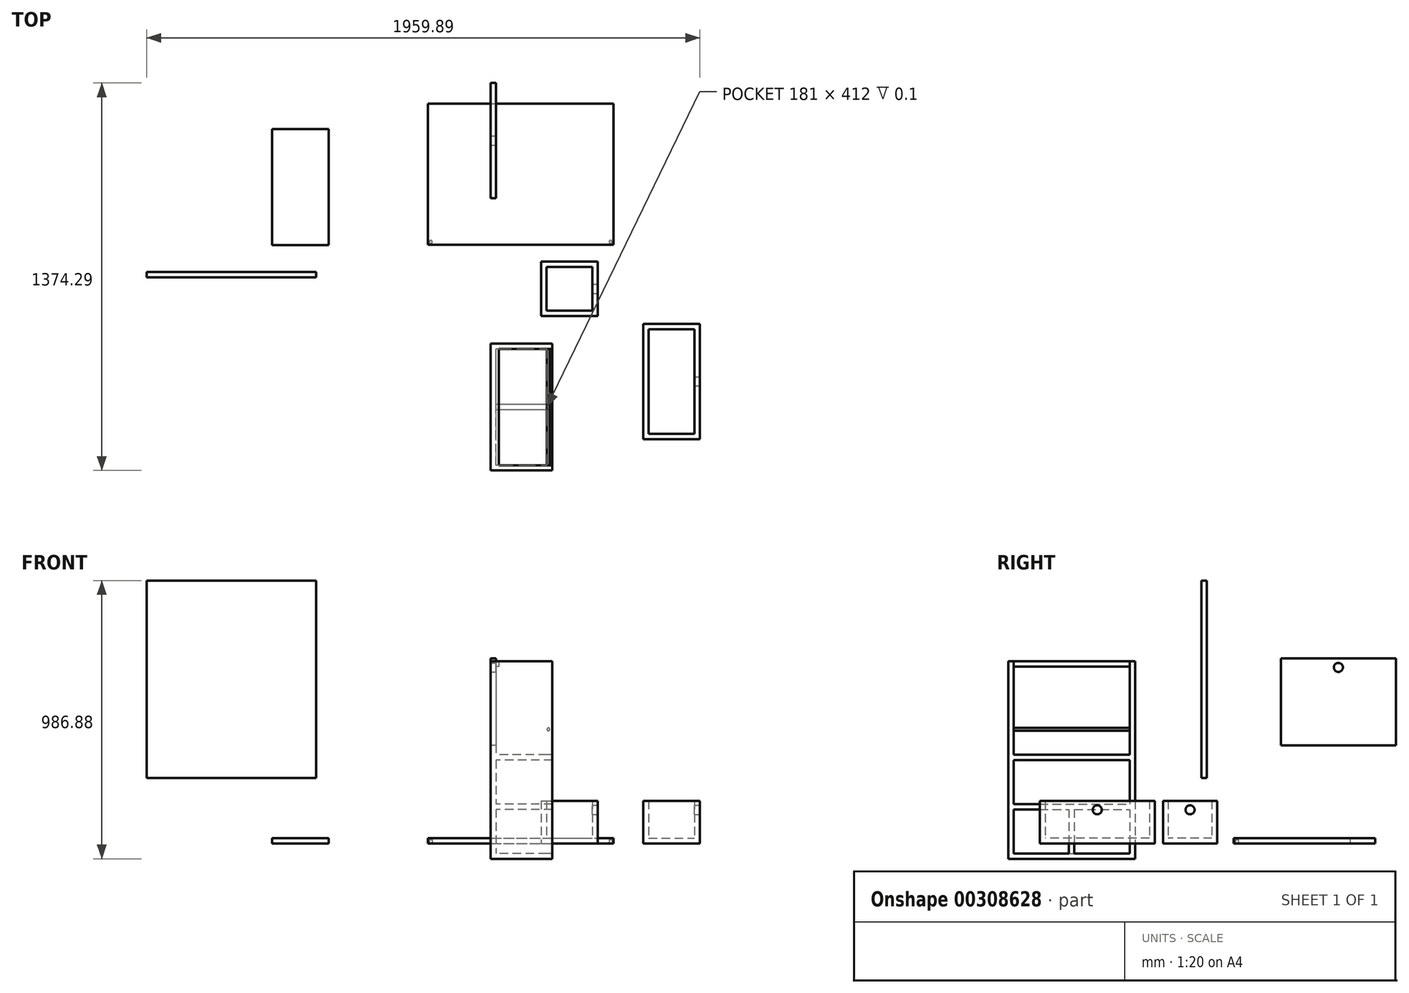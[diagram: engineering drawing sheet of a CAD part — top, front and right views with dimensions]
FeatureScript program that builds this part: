
annotation { "Feature Type Name" : "Feature", "Feature Type Description" : "" }
export const myFeature = defineFeature(function(context is Context, id is Id, definition is map)
    precondition{}
    {
        {
            var Q0;
            Q0=qCreatedBy(makeId("Right.planeOp"),FACE);
            var sketch = newSketch(context, id + "F0", { "sketchPlane" : qUnion([Q0])});
            skLineSegment(sketch, "E0.bottom", {"start": v(-703.87, 646.4) * mm, "end": v(-253.87, 646.4) * mm});
            skLineSegment(sketch, "E0.top", {"start": v(-703.87, -53.6) * mm, "end": v(-253.87, -53.6) * mm});
            skLineSegment(sketch, "E0.left", {"start": v(-703.87, 646.4) * mm, "end": v(-703.87, -53.6) * mm});
            skLineSegment(sketch, "E0.right", {"start": v(-253.87, 646.4) * mm, "end": v(-253.87, -53.6) * mm});
            skSolve(sketch);
        }
        {
            var Q0;
            Q0=qSketchRegion(id+"F0",true);
            extrude(context, id + "F1", {"entities" : qUnion([Q0]), "depth" : 19 * mm});
        }
        {
            var Q0;
            Q0=makeQuery(id+"F1.opExtrude","CAP_FACE",FACE,{"disambiguationData":[OSD([sQuery(id+"F0.wireOp",EDGE,"E0.bottom"),sQuery(id+"F0.wireOp",EDGE,"E0.top"),sQuery(id+"F0.wireOp",EDGE,"E0.left"),sQuery(id+"F0.wireOp",EDGE,"E0.right")])],"isStart":false});
            var sketch = newSketch(context, id + "F2", { "sketchPlane" : qUnion([Q0])});
            skLineSegment(sketch, "E1.bottom", {"start": v(-703.87, 646.4) * mm, "end": v(-684.87, 646.4) * mm});
            skLineSegment(sketch, "E1.top", {"start": v(-703.87, -53.6) * mm, "end": v(-684.87, -53.6) * mm});
            skLineSegment(sketch, "E1.left", {"start": v(-703.87, 646.4) * mm, "end": v(-703.87, -53.6) * mm});
            skLineSegment(sketch, "E1.right", {"start": v(-684.87, 646.4) * mm, "end": v(-684.87, -53.6) * mm});
            skSolve(sketch);
        }
        {
            var Q0;
            Q0=qSketchRegion(id+"F2",true);
            extrude(context, id + "F3", {"entities" : qUnion([Q0]), "operationType" : NewBodyOperationType.ADD, "depth" : 200 * mm});
        }
        {
            var Q0;
            Q0=makeQuery(id+"F1.opExtrude","CAP_FACE",FACE,{"disambiguationData":[OSD([sQuery(id+"F0.wireOp",EDGE,"E0.bottom"),sQuery(id+"F0.wireOp",EDGE,"E0.top"),sQuery(id+"F0.wireOp",EDGE,"E0.left"),sQuery(id+"F0.wireOp",EDGE,"E0.right")])],"isStart":false});
            var sketch = newSketch(context, id + "F4", { "sketchPlane" : qUnion([Q0])});
            skLineSegment(sketch, "E2.bottom", {"start": v(-253.87, 646.4) * mm, "end": v(-272.87, 646.4) * mm});
            skLineSegment(sketch, "E2.top", {"start": v(-253.87, -53.6) * mm, "end": v(-272.87, -53.6) * mm});
            skLineSegment(sketch, "E2.left", {"start": v(-253.87, 646.4) * mm, "end": v(-253.87, -53.6) * mm});
            skLineSegment(sketch, "E2.right", {"start": v(-272.87, 646.4) * mm, "end": v(-272.87, -53.6) * mm});
            skSolve(sketch);
        }
        {
            var Q0;
            Q0=makeQuery(id+"F4.imprint","IMPRINT",FACE,{"disambiguationData":[TD([[makeQuery(id+"F4.imprint","IMPRINT",EDGE,{"derivedFrom":sQuery(id+"F4.wireOp",EDGE,"E2.bottom")}),-1.0]])]});
            extrude(context, id + "F5", {"entities" : qUnion([Q0]), "operationType" : NewBodyOperationType.ADD, "depth" : 200 * mm});
        }
        {
            var Q0;
            Q0=makeQuery(id+"F1.opExtrude","CAP_FACE",FACE,{"disambiguationData":[OSD([sQuery(id+"F0.wireOp",EDGE,"E0.bottom"),sQuery(id+"F0.wireOp",EDGE,"E0.top"),sQuery(id+"F0.wireOp",EDGE,"E0.left"),sQuery(id+"F0.wireOp",EDGE,"E0.right")])],"isStart":false});
            var sketch = newSketch(context, id + "F6", { "sketchPlane" : qUnion([Q0])});
            skLineSegment(sketch, "E3.bottom", {"start": v(-684.87, 646.4) * mm, "end": v(-272.87, 646.4) * mm});
            skLineSegment(sketch, "E3.top", {"start": v(-684.87, 627.4) * mm, "end": v(-272.87, 627.4) * mm});
            skLineSegment(sketch, "E3.left", {"start": v(-684.87, 646.4) * mm, "end": v(-684.87, 627.4) * mm});
            skLineSegment(sketch, "E3.right", {"start": v(-272.87, 646.4) * mm, "end": v(-272.87, 627.4) * mm});
            skSolve(sketch);
        }
        {
            var Q0;
            Q0=makeQuery(id+"F6.imprint","IMPRINT",FACE,{"disambiguationData":[TD([[makeQuery(id+"F6.imprint","IMPRINT",EDGE,{"derivedFrom":sQuery(id+"F6.wireOp",EDGE,"E3.bottom")}),-1.0]])]});
            extrude(context, id + "F7", {"entities" : qUnion([Q0]), "operationType" : NewBodyOperationType.ADD, "depth" : 10 * mm});
        }
        {
            var Q0;
            Q0=makeQuery(id+"F1.opExtrude","CAP_FACE",FACE,{"disambiguationData":[OSD([sQuery(id+"F0.wireOp",EDGE,"E0.bottom"),sQuery(id+"F0.wireOp",EDGE,"E0.top"),sQuery(id+"F0.wireOp",EDGE,"E0.left"),sQuery(id+"F0.wireOp",EDGE,"E0.right")])],"isStart":false});
            var sketch = newSketch(context, id + "F8", { "sketchPlane" : qUnion([Q0])});
            skLineSegment(sketch, "E4.bottom", {"start": v(-684.87, -53.6) * mm, "end": v(-272.87, -53.6) * mm});
            skLineSegment(sketch, "E4.top", {"start": v(-684.87, -34.6) * mm, "end": v(-272.87, -34.6) * mm});
            skLineSegment(sketch, "E4.left", {"start": v(-684.87, -53.6) * mm, "end": v(-684.87, -34.6) * mm});
            skLineSegment(sketch, "E4.right", {"start": v(-272.87, -53.6) * mm, "end": v(-272.87, -34.6) * mm});
            skSolve(sketch);
        }
        {
            var Q0;
            Q0=qSketchRegion(id+"F8",true);
            extrude(context, id + "F9", {"entities" : qUnion([Q0]), "operationType" : NewBodyOperationType.ADD, "depth" : 200 * mm});
        }
        {
            var Q0;
            Q0=makeQuery(id+"F9.opExtrude","SWEPT_FACE",FACE,{"disambiguationData":[OSD([sQuery(id+"F8.wireOp",EDGE,"E4.top")])]});
            var sketch = newSketch(context, id + "F10", { "sketchPlane" : qUnion([Q0])});
            skLineSegment(sketch, "E5.bottom", {"start": v(219, -684.87) * mm, "end": v(200, -684.87) * mm});
            skLineSegment(sketch, "E5.top", {"start": v(219, -272.87) * mm, "end": v(200, -272.87) * mm});
            skLineSegment(sketch, "E5.left", {"start": v(219, -684.87) * mm, "end": v(219, -272.87) * mm});
            skLineSegment(sketch, "E5.right", {"start": v(200, -684.87) * mm, "end": v(200, -272.87) * mm});
            skSolve(sketch);
        }
        {
            var Q0;
            Q0=qSketchRegion(id+"F10",true);
            extrude(context, id + "F11", {"entities" : qUnion([Q0]), "operationType" : NewBodyOperationType.ADD, "depth" : 0.1 * mm});
        }
        {
            var Q0;
            Q0=makeQuery(id+"F1.opExtrude","CAP_FACE",FACE,{"disambiguationData":[OSD([sQuery(id+"F0.wireOp",EDGE,"E0.bottom"),sQuery(id+"F0.wireOp",EDGE,"E0.top"),sQuery(id+"F0.wireOp",EDGE,"E0.left"),sQuery(id+"F0.wireOp",EDGE,"E0.right")])],"isStart":false});
            var sketch = newSketch(context, id + "F12", { "sketchPlane" : qUnion([Q0])});
            skLineSegment(sketch, "E6.bottom", {"start": v(-684.87, 296.4) * mm, "end": v(-272.87, 296.4) * mm});
            skLineSegment(sketch, "E6.top", {"start": v(-684.87, 315.4) * mm, "end": v(-272.87, 315.4) * mm});
            skLineSegment(sketch, "E6.left", {"start": v(-684.87, 296.4) * mm, "end": v(-684.87, 315.4) * mm});
            skLineSegment(sketch, "E6.right", {"start": v(-272.87, 296.4) * mm, "end": v(-272.87, 315.4) * mm});
            skSolve(sketch);
        }
        {
            var Q0;
            Q0=qSketchRegion(id+"F12",true);
            extrude(context, id + "F13", {"entities" : qUnion([Q0]), "operationType" : NewBodyOperationType.ADD, "depth" : 200 * mm});
        }
        {
            var Q0;
            Q0=makeQuery(id+"F13.opExtrude","SWEPT_FACE",FACE,{"disambiguationData":[OSD([sQuery(id+"F12.wireOp",EDGE,"E6.top")])]});
            var sketch = newSketch(context, id + "F14", { "sketchPlane" : qUnion([Q0])});
            skLineSegment(sketch, "E7.bottom", {"start": v(219, -272.87) * mm, "end": v(200, -272.87) * mm});
            skLineSegment(sketch, "E7.top", {"start": v(219, -684.87) * mm, "end": v(200, -684.87) * mm});
            skLineSegment(sketch, "E7.left", {"start": v(219, -272.87) * mm, "end": v(219, -684.87) * mm});
            skLineSegment(sketch, "E7.right", {"start": v(200, -272.87) * mm, "end": v(200, -684.87) * mm});
            skSolve(sketch);
        }
        {
            var Q0;
            Q0=qSketchRegion(id+"F14",true);
            extrude(context, id + "F15", {"entities" : qUnion([Q0]), "operationType" : NewBodyOperationType.ADD, "depth" : 0.1 * mm});
        }
        {
            var Q0;
            Q0=qCreatedBy(makeId("Top.planeOp"),FACE);
            var sketch = newSketch(context, id + "F16", { "sketchPlane" : qUnion([Q0])});
            skLineSegment(sketch, "E8.bottom", {"start": v(-221.88, 597.16) * mm, "end": v(435.12, 597.16) * mm});
            skLineSegment(sketch, "E8.top", {"start": v(-221.88, 97.16) * mm, "end": v(435.12, 97.16) * mm});
            skLineSegment(sketch, "E8.left", {"start": v(-221.88, 597.16) * mm, "end": v(-221.88, 97.16) * mm});
            skLineSegment(sketch, "E8.right", {"start": v(435.12, 597.16) * mm, "end": v(435.12, 97.16) * mm});
            skSolve(sketch);
        }
        {
            var Q0;
            Q0=makeQuery(id+"F16.imprint","IMPRINT",FACE,{"disambiguationData":[TD([[makeQuery(id+"F16.imprint","IMPRINT",EDGE,{"derivedFrom":sQuery(id+"F16.wireOp",EDGE,"E8.bottom")}),-1.0]])]});
            extrude(context, id + "F17", {"entities" : qUnion([Q0]), "depth" : 19 * mm});
        }
        {
            var Q0;
            Q0=qCreatedBy(makeId("Front.planeOp"),FACE);
            var sketch = newSketch(context, id + "F18", { "sketchPlane" : qUnion([Q0])});
            skLineSegment(sketch, "E9.bottom", {"start": v(-1218.5, 933.28) * mm, "end": v(-618.5, 933.28) * mm});
            skLineSegment(sketch, "E9.top", {"start": v(-1218.5, 233.28) * mm, "end": v(-618.5, 233.28) * mm});
            skLineSegment(sketch, "E9.left", {"start": v(-1218.5, 933.28) * mm, "end": v(-1218.5, 233.28) * mm});
            skLineSegment(sketch, "E9.right", {"start": v(-618.5, 933.28) * mm, "end": v(-618.5, 233.28) * mm});
            skSolve(sketch);
        }
        {
            var Q0;
            Q0=qSketchRegion(id+"F18",true);
            extrude(context, id + "F19", {"entities" : qUnion([Q0]), "depth" : 19 * mm});
        }
        {
            var Q0;
            Q0=makeQuery(id+"F7.boolean.opBoolean","MERGE",FACE,{"derivedFrom":[makeQuery(id+"F5.boolean.opBoolean","MERGE",FACE,{"derivedFrom":[makeQuery(id+"F3.boolean.opBoolean","MERGE",FACE,{"derivedFrom":[makeQuery(id+"F1.opExtrude","SWEPT_FACE",FACE,{"disambiguationData":[OSD([sQuery(id+"F0.wireOp",EDGE,"E0.bottom")])]}),makeQuery(id+"F3.opExtrude","SWEPT_FACE",FACE,{"disambiguationData":[OSD([sQuery(id+"F2.wireOp",EDGE,"E1.bottom")])]})]}),makeQuery(id+"F5.opExtrude","SWEPT_FACE",FACE,{"disambiguationData":[OSD([sQuery(id+"F4.wireOp",EDGE,"E2.bottom")])]})]}),makeQuery(id+"F7.opExtrude","SWEPT_FACE",FACE,{"disambiguationData":[OSD([sQuery(id+"F6.wireOp",EDGE,"E3.bottom")])]})]});
            var sketch = newSketch(context, id + "F20", { "sketchPlane" : qUnion([Q0])});
            skCircle(sketch, "E10", {"center": v(169, -303.87) * mm, "radius": 5 * mm});
            skSolve(sketch);
        }
        {
            var Q0;
            Q0=makeQuery(id+"F20.imprint","IMPRINT",FACE,{"disambiguationData":[TD([[makeQuery(id+"F20.imprint","IMPRINT",EDGE,{"derivedFrom":sQuery(id+"F20.wireOp",EDGE,"E10")}),1.0]])]});
            extrude(context, id + "F21", {"entities" : qUnion([Q0]), "operationType" : NewBodyOperationType.REMOVE, "oppositeDirection" : true, "depth" : 15 * mm});
        }
        {
            var Q0;
            Q0=makeQuery(id+"F17.opExtrude","CAP_FACE",FACE,{"disambiguationData":[OSD([sQuery(id+"F16.wireOp",EDGE,"E8.bottom"),sQuery(id+"F16.wireOp",EDGE,"E8.top"),sQuery(id+"F16.wireOp",EDGE,"E8.left"),sQuery(id+"F16.wireOp",EDGE,"E8.right")])],"isStart":true});
            var sketch = newSketch(context, id + "F22", { "sketchPlane" : qUnion([Q0])});
            skCircle(sketch, "E11", {"center": v(425.12, -107.16) * mm, "radius": 5 * mm});
            skSolve(sketch);
        }
        {
            var Q0;
            Q0=qSketchRegion(id+"F22",true);
            extrude(context, id + "F23", {"entities" : qUnion([Q0]), "operationType" : NewBodyOperationType.REMOVE, "oppositeDirection" : true, "depth" : 15 * mm});
        }
        {
            var Q0;
            Q0=makeQuery(id+"F7.boolean.opBoolean","MERGE",FACE,{"derivedFrom":[makeQuery(id+"F5.boolean.opBoolean","MERGE",FACE,{"derivedFrom":[makeQuery(id+"F3.boolean.opBoolean","MERGE",FACE,{"derivedFrom":[makeQuery(id+"F1.opExtrude","SWEPT_FACE",FACE,{"disambiguationData":[OSD([sQuery(id+"F0.wireOp",EDGE,"E0.bottom")])]}),makeQuery(id+"F3.opExtrude","SWEPT_FACE",FACE,{"disambiguationData":[OSD([sQuery(id+"F2.wireOp",EDGE,"E1.bottom")])]})]}),makeQuery(id+"F5.opExtrude","SWEPT_FACE",FACE,{"disambiguationData":[OSD([sQuery(id+"F4.wireOp",EDGE,"E2.bottom")])]})]}),makeQuery(id+"F7.opExtrude","SWEPT_FACE",FACE,{"disambiguationData":[OSD([sQuery(id+"F6.wireOp",EDGE,"E3.bottom")])]})]});
            var sketch = newSketch(context, id + "F24", { "sketchPlane" : qUnion([Q0])});
            skCircle(sketch, "E12", {"center": v(169, -653.87) * mm, "radius": 5 * mm});
            skSolve(sketch);
        }
        {
            var Q0;
            Q0=makeQuery(id+"F24.imprint","IMPRINT",FACE,{"disambiguationData":[TD([[makeQuery(id+"F24.imprint","IMPRINT",EDGE,{"derivedFrom":sQuery(id+"F24.wireOp",EDGE,"E12")}),1.0]])]});
            extrude(context, id + "F25", {"entities" : qUnion([Q0]), "operationType" : NewBodyOperationType.REMOVE, "oppositeDirection" : true, "depth" : 15 * mm});
        }
        {
            var Q0;
            Q0=makeQuery(id+"F17.opExtrude","CAP_FACE",FACE,{"disambiguationData":[OSD([sQuery(id+"F16.wireOp",EDGE,"E8.bottom"),sQuery(id+"F16.wireOp",EDGE,"E8.top"),sQuery(id+"F16.wireOp",EDGE,"E8.left"),sQuery(id+"F16.wireOp",EDGE,"E8.right")])],"isStart":true});
            var sketch = newSketch(context, id + "F26", { "sketchPlane" : qUnion([Q0])});
            skCircle(sketch, "E13", {"center": v(-211.88, -107.16) * mm, "radius": 5 * mm});
            skSolve(sketch);
        }
        {
            var Q0;
            Q0=makeQuery(id+"F26.imprint","IMPRINT",FACE,{"disambiguationData":[TD([[makeQuery(id+"F26.imprint","IMPRINT",EDGE,{"derivedFrom":sQuery(id+"F26.wireOp",EDGE,"E13")}),1.0]])]});
            extrude(context, id + "F27", {"entities" : qUnion([Q0]), "operationType" : NewBodyOperationType.REMOVE, "oppositeDirection" : true, "depth" : 15 * mm});
        }
        {
            var Q0;
            {var subQ0=sQuery(id+"F4.wireOp",EDGE,"E2.right");var subQ3=sQuery(id+"F0.wireOp",EDGE,"E0.bottom");Q0=makeQuery(id+"F13.boolean.opBoolean","SPLIT",FACE,{"disambiguationData":[TD([makeQuery(id+"F1.opExtrude","SWEPT_FACE",FACE,{"disambiguationData":[OSD([subQ3])]})])],"derivedFrom":makeQuery(id+"F5.opExtrude","SWEPT_FACE",FACE,{"disambiguationData":[OSD([subQ0])]})});}
            var sketch = newSketch(context, id + "F28", { "sketchPlane" : qUnion([Q0])});
            skCircle(sketch, "E14", {"center": v(205, 405.5) * mm, "radius": 5 * mm});
            skSolve(sketch);
        }
        {
            var Q0;
            Q0=makeQuery(id+"F28.imprint","IMPRINT",FACE,{"disambiguationData":[TD([[makeQuery(id+"F28.imprint","IMPRINT",EDGE,{"derivedFrom":sQuery(id+"F28.wireOp",EDGE,"E14")}),1.0]])]});
            extrude(context, id + "F29", {"entities" : qUnion([Q0]), "operationType" : NewBodyOperationType.ADD, "depth" : 430 * mm});
        }
        {
            var Q0;
            Q0=makeQuery(id+"F13.boolean.opBoolean","SPLIT",FACE,{"disambiguationData":[TD([makeQuery(id+"F9.opExtrude","SWEPT_FACE",FACE,{"disambiguationData":[OSD([sQuery(id+"F8.wireOp",EDGE,"E4.top")])]})])],"derivedFrom":makeQuery(id+"F1.opExtrude","CAP_FACE",FACE,{"disambiguationData":[OSD([sQuery(id+"F0.wireOp",EDGE,"E0.bottom"),sQuery(id+"F0.wireOp",EDGE,"E0.top"),sQuery(id+"F0.wireOp",EDGE,"E0.left"),sQuery(id+"F0.wireOp",EDGE,"E0.right")])],"isStart":false})});
            var sketch = newSketch(context, id + "F30", { "sketchPlane" : qUnion([Q0])});
            skLineSegment(sketch, "E15.bottom", {"start": v(-684.87, 121.45) * mm, "end": v(-272.87, 121.45) * mm});
            skLineSegment(sketch, "E15.top", {"start": v(-684.87, 140.45) * mm, "end": v(-272.87, 140.45) * mm});
            skLineSegment(sketch, "E15.left", {"start": v(-684.87, 121.45) * mm, "end": v(-684.87, 140.45) * mm});
            skLineSegment(sketch, "E15.right", {"start": v(-272.87, 121.45) * mm, "end": v(-272.87, 140.45) * mm});
            skSolve(sketch);
        }
        {
            var Q0;
            Q0=qSketchRegion(id+"F30",true);
            var Q1;
            Q1=makeQuery(id+"F30.imprint","IMPRINT",FACE,{"disambiguationData":[TD([[makeQuery(id+"F30.imprint","IMPRINT",EDGE,{"derivedFrom":sQuery(id+"F30.wireOp",EDGE,"E15.bottom")}),1.0]])]});
            extrude(context, id + "F31", {"entities" : qUnion([Q0, Q1]), "operationType" : NewBodyOperationType.ADD, "depth" : 200 * mm});
        }
        {
            var Q0;
            {var subQ1=makeQuery(id+"F13.opExtrude","SWEPT_FACE",FACE,{"disambiguationData":[OSD([sQuery(id+"F12.wireOp",EDGE,"E6.bottom")])]});Q0=makeQuery(id+"F31.boolean.opBoolean","SPLIT",FACE,{"disambiguationData":[TD([subQ1])],"derivedFrom":makeQuery(id+"F13.boolean.opBoolean","SPLIT",FACE,{"disambiguationData":[TD([makeQuery(id+"F9.opExtrude","SWEPT_FACE",FACE,{"disambiguationData":[OSD([sQuery(id+"F8.wireOp",EDGE,"E4.top")])]})])],"derivedFrom":makeQuery(id+"F1.opExtrude","CAP_FACE",FACE,{"disambiguationData":[OSD([sQuery(id+"F0.wireOp",EDGE,"E0.bottom"),sQuery(id+"F0.wireOp",EDGE,"E0.top"),sQuery(id+"F0.wireOp",EDGE,"E0.left"),sQuery(id+"F0.wireOp",EDGE,"E0.right")])],"isStart":false})})});}
            var sketch = newSketch(context, id + "F32", { "sketchPlane" : qUnion([Q0])});
            skLineSegment(sketch, "E16.bottom", {"start": v(-488.37, 296.4) * mm, "end": v(-469.37, 296.4) * mm});
            skLineSegment(sketch, "E16.top", {"start": v(-488.37, -34.5) * mm, "end": v(-469.37, -34.5) * mm});
            skLineSegment(sketch, "E16.left", {"start": v(-488.37, 296.4) * mm, "end": v(-488.37, -34.5) * mm});
            skLineSegment(sketch, "E16.right", {"start": v(-469.37, 296.4) * mm, "end": v(-469.37, -34.5) * mm});
            skSolve(sketch);
        }
        {
            var Q0;
            {var subQ0=sQuery(id+"F32.wireOp",EDGE,"E16.top");Q0=makeQuery(id+"F32.imprint","IMPRINT",FACE,{"disambiguationData":[TD([[makeQuery(id+"F32.imprint","IMPRINT",EDGE,{"derivedFrom":subQ0}),1.0]])]});}
            extrude(context, id + "F33", {"entities" : qUnion([Q0]), "operationType" : NewBodyOperationType.ADD, "depth" : 200 * mm});
        }
        {
            var Q0;
            Q0=qCreatedBy(makeId("Top.planeOp"),FACE);
            var sketch = newSketch(context, id + "F34", { "sketchPlane" : qUnion([Q0])});
            skLineSegment(sketch, "E17.bottom", {"start": v(179.4, 36.97) * mm, "end": v(379.4, 36.97) * mm});
            skLineSegment(sketch, "E17.top", {"start": v(179.4, -155.53) * mm, "end": v(379.4, -155.53) * mm});
            skLineSegment(sketch, "E17.left", {"start": v(179.4, 36.97) * mm, "end": v(179.4, -155.53) * mm});
            skLineSegment(sketch, "E17.right", {"start": v(379.4, 36.97) * mm, "end": v(379.4, -155.53) * mm});
            skSolve(sketch);
        }
        {
            var Q0;
            Q0=qSketchRegion(id+"F34",true);
            extrude(context, id + "F35", {"entities" : qUnion([Q0]), "depth" : 19 * mm});
        }
        {
            var Q0;
            Q0=makeQuery(id+"F35.opExtrude","CAP_FACE",FACE,{"disambiguationData":[OSD([sQuery(id+"F34.wireOp",EDGE,"E17.bottom"),sQuery(id+"F34.wireOp",EDGE,"E17.top"),sQuery(id+"F34.wireOp",EDGE,"E17.left"),sQuery(id+"F34.wireOp",EDGE,"E17.right")])],"isStart":false});
            var sketch = newSketch(context, id + "F36", { "sketchPlane" : qUnion([Q0])});
            skLineSegment(sketch, "E18.bottom", {"start": v(179.4, 36.97) * mm, "end": v(379.4, 36.97) * mm});
            skLineSegment(sketch, "E18.top", {"start": v(179.4, -155.53) * mm, "end": v(379.4, -155.53) * mm});
            skLineSegment(sketch, "E18.left", {"start": v(179.4, 36.97) * mm, "end": v(179.4, -155.53) * mm});
            skLineSegment(sketch, "E18.right", {"start": v(379.4, 36.97) * mm, "end": v(379.4, -155.53) * mm});
            skLineSegment(sketch, "E19.bottom", {"start": v(198.4, 17.97) * mm, "end": v(360.4, 17.97) * mm});
            skLineSegment(sketch, "E19.top", {"start": v(198.4, -136.53) * mm, "end": v(360.4, -136.53) * mm});
            skLineSegment(sketch, "E19.left", {"start": v(198.4, 17.97) * mm, "end": v(198.4, -136.53) * mm});
            skLineSegment(sketch, "E19.right", {"start": v(360.4, 17.97) * mm, "end": v(360.4, -136.53) * mm});
            skSolve(sketch);
        }
        {
            var Q0;
            Q0=makeQuery(id+"F36.imprint","IMPRINT",FACE,{"disambiguationData":[TD([[makeQuery(id+"F36.imprint","IMPRINT",EDGE,{"derivedFrom":sQuery(id+"F36.wireOp",EDGE,"E18.bottom")}),-1.0]])]});
            extrude(context, id + "F37", {"entities" : qUnion([Q0]), "operationType" : NewBodyOperationType.ADD, "depth" : 132.95 * mm});
        }
        {
            var Q0;
            Q0=makeQuery(id+"F37.boolean.opBoolean","MERGE",FACE,{"derivedFrom":[makeQuery(id+"F35.opExtrude","SWEPT_FACE",FACE,{"disambiguationData":[OSD([sQuery(id+"F34.wireOp",EDGE,"E17.right")])]}),makeQuery(id+"F37.opExtrude","SWEPT_FACE",FACE,{"disambiguationData":[OSD([sQuery(id+"F36.wireOp",EDGE,"E18.right")])]})]});
            var sketch = newSketch(context, id + "F38", { "sketchPlane" : qUnion([Q0])});
            skCircle(sketch, "E20", {"center": v(-59.28, 119.95) * mm, "radius": 16 * mm});
            skPoint(sketch, "E20.centerSnap0", {"position": v(-59.28, 151.95) * mm});
            skSolve(sketch);
        }
        {
            var Q0;
            Q0=makeQuery(id+"F38.imprint","IMPRINT",FACE,{"disambiguationData":[TD([[makeQuery(id+"F38.imprint","IMPRINT",EDGE,{"derivedFrom":sQuery(id+"F38.wireOp",EDGE,"E20")}),1.0]])]});
            extrude(context, id + "F39", {"entities" : qUnion([Q0]), "operationType" : NewBodyOperationType.REMOVE, "oppositeDirection" : true, "depth" : 25 * mm});
        }
        {
            var Q0;
            Q0=qCreatedBy(makeId("Top.planeOp"),FACE);
            var sketch = newSketch(context, id + "F40", { "sketchPlane" : qUnion([Q0])});
            skLineSegment(sketch, "E21.bottom", {"start": v(541.4, -184.16) * mm, "end": v(741.4, -184.16) * mm});
            skLineSegment(sketch, "E21.top", {"start": v(541.4, -592.16) * mm, "end": v(741.4, -592.16) * mm});
            skLineSegment(sketch, "E21.left", {"start": v(541.4, -184.16) * mm, "end": v(541.4, -592.16) * mm});
            skLineSegment(sketch, "E21.right", {"start": v(741.4, -184.16) * mm, "end": v(741.4, -592.16) * mm});
            skSolve(sketch);
        }
        {
            var Q0;
            Q0=makeQuery(id+"F40.imprint","IMPRINT",FACE,{"disambiguationData":[TD([[makeQuery(id+"F40.imprint","IMPRINT",EDGE,{"derivedFrom":sQuery(id+"F40.wireOp",EDGE,"E21.bottom")}),-1.0]])]});
            extrude(context, id + "F41", {"entities" : qUnion([Q0]), "depth" : 19 * mm});
        }
        {
            var Q0;
            Q0=makeQuery(id+"F41.opExtrude","CAP_FACE",FACE,{"disambiguationData":[OSD([sQuery(id+"F40.wireOp",EDGE,"E21.bottom"),sQuery(id+"F40.wireOp",EDGE,"E21.top"),sQuery(id+"F40.wireOp",EDGE,"E21.left"),sQuery(id+"F40.wireOp",EDGE,"E21.right")])],"isStart":false});
            var sketch = newSketch(context, id + "F42", { "sketchPlane" : qUnion([Q0])});
            skLineSegment(sketch, "E22.bottom", {"start": v(541.4, -184.16) * mm, "end": v(741.4, -184.16) * mm});
            skLineSegment(sketch, "E22.top", {"start": v(541.4, -592.16) * mm, "end": v(741.4, -592.16) * mm});
            skLineSegment(sketch, "E22.left", {"start": v(541.4, -184.16) * mm, "end": v(541.4, -592.16) * mm});
            skLineSegment(sketch, "E22.right", {"start": v(741.4, -184.16) * mm, "end": v(741.4, -592.16) * mm});
            skLineSegment(sketch, "E23.bottom", {"start": v(560.4, -203.16) * mm, "end": v(722.4, -203.16) * mm});
            skLineSegment(sketch, "E23.top", {"start": v(560.4, -573.16) * mm, "end": v(722.4, -573.16) * mm});
            skLineSegment(sketch, "E23.left", {"start": v(560.4, -203.16) * mm, "end": v(560.4, -573.16) * mm});
            skLineSegment(sketch, "E23.right", {"start": v(722.4, -203.16) * mm, "end": v(722.4, -573.16) * mm});
            skSolve(sketch);
        }
        {
            var Q0;
            Q0=makeQuery(id+"F42.imprint","IMPRINT",FACE,{"disambiguationData":[TD([[makeQuery(id+"F42.imprint","IMPRINT",EDGE,{"derivedFrom":sQuery(id+"F42.wireOp",EDGE,"E22.bottom")}),-1.0]])]});
            extrude(context, id + "F43", {"entities" : qUnion([Q0]), "operationType" : NewBodyOperationType.ADD, "depth" : 132.95 * mm});
        }
        {
            var Q0;
            Q0=makeQuery(id+"F43.boolean.opBoolean","MERGE",FACE,{"derivedFrom":[makeQuery(id+"F41.opExtrude","SWEPT_FACE",FACE,{"disambiguationData":[OSD([sQuery(id+"F40.wireOp",EDGE,"E21.right")])]}),makeQuery(id+"F43.opExtrude","SWEPT_FACE",FACE,{"disambiguationData":[OSD([sQuery(id+"F42.wireOp",EDGE,"E22.right")])]})]});
            var sketch = newSketch(context, id + "F44", { "sketchPlane" : qUnion([Q0])});
            skCircle(sketch, "E24", {"center": v(-388.16, 119.95) * mm, "radius": 16 * mm});
            skPoint(sketch, "E24.centerSnap0", {"position": v(-388.16, 151.95) * mm});
            skSolve(sketch);
        }
        {
            var Q0;
            Q0=makeQuery(id+"F44.imprint","IMPRINT",FACE,{"disambiguationData":[TD([[makeQuery(id+"F44.imprint","IMPRINT",EDGE,{"derivedFrom":sQuery(id+"F44.wireOp",EDGE,"E24")}),1.0]])]});
            extrude(context, id + "F45", {"entities" : qUnion([Q0]), "operationType" : NewBodyOperationType.REMOVE, "oppositeDirection" : true, "depth" : 25 * mm});
        }
        {
            var Q0;
            Q0=qCreatedBy(makeId("Right.planeOp"),FACE);
            var sketch = newSketch(context, id + "F46", { "sketchPlane" : qUnion([Q0])});
            skLineSegment(sketch, "E25.bottom", {"start": v(262.42, 657.06) * mm, "end": v(670.42, 657.06) * mm});
            skLineSegment(sketch, "E25.top", {"start": v(262.42, 349.06) * mm, "end": v(670.42, 349.06) * mm});
            skLineSegment(sketch, "E25.left", {"start": v(262.42, 657.06) * mm, "end": v(262.42, 349.06) * mm});
            skLineSegment(sketch, "E25.right", {"start": v(670.42, 657.06) * mm, "end": v(670.42, 349.06) * mm});
            skSolve(sketch);
        }
        {
            var Q0;
            Q0=qSketchRegion(id+"F46",true);
            extrude(context, id + "F47", {"entities" : qUnion([Q0]), "depth" : 19 * mm});
        }
        {
            var Q0;
            Q0=makeQuery(id+"F47.opExtrude","CAP_FACE",FACE,{"disambiguationData":[OSD([sQuery(id+"F46.wireOp",EDGE,"E25.bottom"),sQuery(id+"F46.wireOp",EDGE,"E25.top"),sQuery(id+"F46.wireOp",EDGE,"E25.left"),sQuery(id+"F46.wireOp",EDGE,"E25.right")])],"isStart":false});
            var sketch = newSketch(context, id + "F48", { "sketchPlane" : qUnion([Q0])});
            skCircle(sketch, "E26", {"center": v(466.42, 625.06) * mm, "radius": 16 * mm});
            skPoint(sketch, "E26.centerSnap0", {"position": v(466.42, 657.06) * mm});
            skSolve(sketch);
        }
        {
            var Q0;
            Q0=makeQuery(id+"F48.imprint","IMPRINT",FACE,{"disambiguationData":[TD([[makeQuery(id+"F48.imprint","IMPRINT",EDGE,{"derivedFrom":sQuery(id+"F48.wireOp",EDGE,"E26")}),1.0]])]});
            extrude(context, id + "F49", {"entities" : qUnion([Q0]), "operationType" : NewBodyOperationType.REMOVE, "oppositeDirection" : true, "depth" : 25 * mm});
        }
        {
            var Q0;
            Q0=qCreatedBy(makeId("Top.planeOp"),FACE);
            var sketch = newSketch(context, id + "F50", { "sketchPlane" : qUnion([Q0])});
            skLineSegment(sketch, "E27.bottom", {"start": v(-774.22, 507.65) * mm, "end": v(-574.22, 507.65) * mm});
            skLineSegment(sketch, "E27.top", {"start": v(-774.22, 95.65) * mm, "end": v(-574.22, 95.65) * mm});
            skLineSegment(sketch, "E27.left", {"start": v(-774.22, 507.65) * mm, "end": v(-774.22, 95.65) * mm});
            skLineSegment(sketch, "E27.right", {"start": v(-574.22, 507.65) * mm, "end": v(-574.22, 95.65) * mm});
            skSolve(sketch);
        }
        {
            var Q0;
            Q0=qSketchRegion(id+"F50",true);
            extrude(context, id + "F51", {"entities" : qUnion([Q0]), "depth" : 19 * mm});
        }
    });
